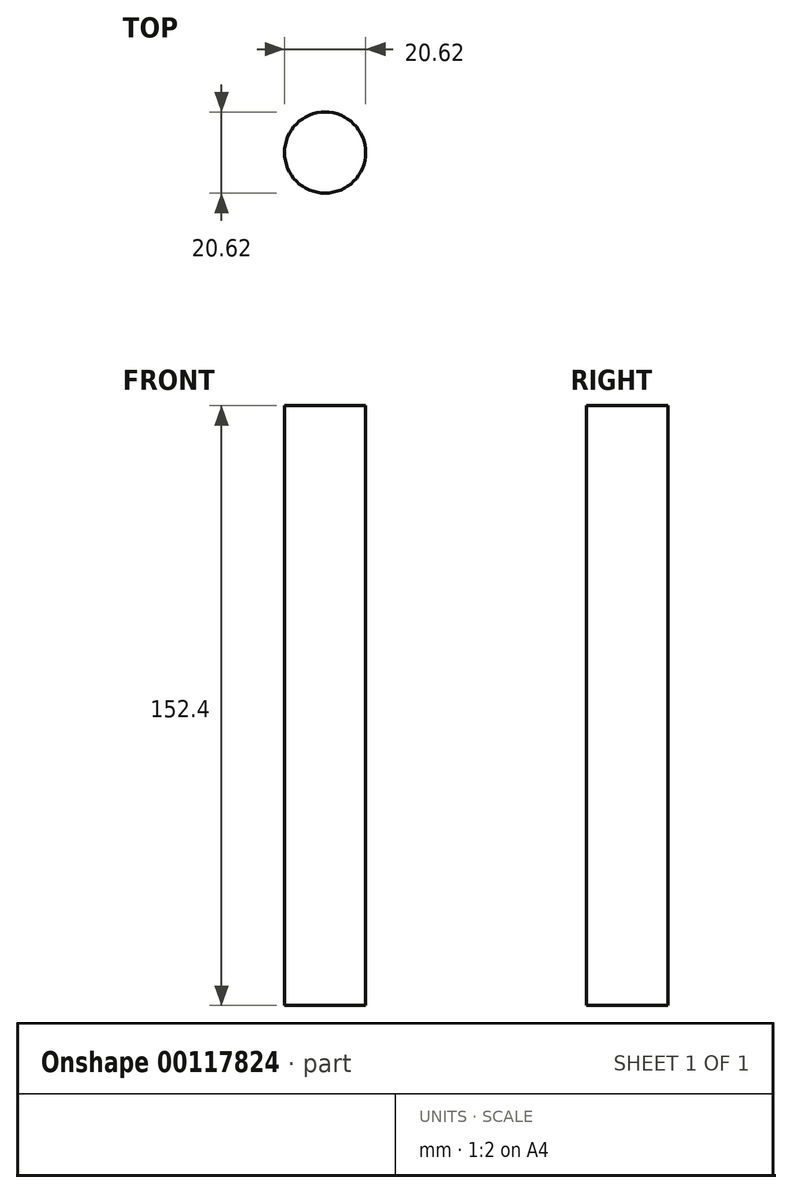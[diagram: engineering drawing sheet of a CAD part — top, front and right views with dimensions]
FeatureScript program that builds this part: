
annotation { "Feature Type Name" : "Feature", "Feature Type Description" : "" }
export const myFeature = defineFeature(function(context is Context, id is Id, definition is map)
    precondition{}
    {
        {
            var Q0;
            Q0=qCreatedBy(makeId("Top.planeOp"),FACE);
            var sketch = newSketch(context, id + "F0", { "sketchPlane" : qUnion([Q0])});
            skCircle(sketch, "E0", {"center": v(0, 0) * mm, "radius": 10.3 * mm});
            skSolve(sketch);
        }
        {
            var Q0;
            Q0 = qSketchRegion(id + "F0", true);
            extrude(context, id + "F1", {"entities" : qUnion([Q0]), "endBound" : BoundingType.SYMMETRIC, "depth" : 152.4 * mm});
        }
    });
